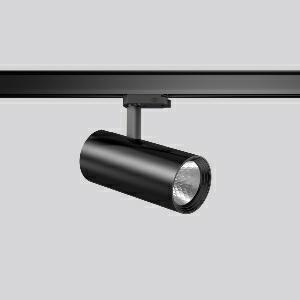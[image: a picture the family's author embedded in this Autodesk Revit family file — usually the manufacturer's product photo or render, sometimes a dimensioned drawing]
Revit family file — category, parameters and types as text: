
# Revit family: deecos_s_mini_742196_003_76_2dde
name_source: partatom
category: Lighting Fixtures
units: mm (PartAtom-declared; Revit-internal decimal feet)

## family parameters
Cut with Voids When Loaded = No
Host = Face
Light Source = No
Part Type = Normal
Room Calculation Point = No
Round Connector Dimension = Use Diameter
Shared = No

## types (1)
- DEECOS S mini (1 x LED Modul 930, 2450 lm, 3000)
    Apparent Load = 20 VA
    Approval mark = CE
    CIE Flux Codes = 99 100 100 100 100
    Color Rendering = 90
    Color Temperature = 3000
    Default Elevation = 1800 mm
    Description = Series: DEECOS S mini
LED surface-mounted projector in modern design with no visible cooling ribs. Housing: die-cast aluminium, powder-coated. Rotation range: 356°. Swivel range: 90°. Black plastic ring and recessed LED to prevent glare from the side. Optical assembly with reflector made of MIRO-Silver with 98% total light reflection for outstanding efficiency - can be changed without tools. Best colour rendering index Ra>90. With adapter for RZB 3-circuit DALI tracks. Suitable for Track on ceiling, Wall track. High quality converter without flickering and stroboscopic effect. The following accessories can be mounted without use of tools: interchangeable lenses, decorative glasses, honeycomb louvre, clear and frosted diffusers, white interchangeable plastic ring. 
Colour: deep black, matt (RAL 9005)
Diameter: 87 mm
Height: 214 mm
Lamp: LED
Socket: without socket
Colour temperature: 3000K
Colour rendering index (CRI): 92
System power: 20 W
Rated luminous flux: 2450 lm
Luminous efficiency: 123 lm/W
Control gear: Converter, dimmable, DALI
Protection class: I
Type of protection: IP 20
    Height = 214 mm
    Lamp = 1 x LED Modul 930
    Lamp Light Flux = 2450 lm
    Lamp count = 1
    Length = 87 mm
    Lifetime = 50000 h
    Luminous efficacy = 123 lm/W
    Manufacturer = RZB
    ModVariant = No
    Model = 742196.003.76
    Mounting Place = Ceiling
    Mounting Type = Rail mounted
    Number of Poles = 1
    OnlyDefault = Yes
    Power Factor = 1
    Product Name = DEECOS S mini
    Product group = Track mounted projectors
    ProductGroupID = 301
    Protection Class = Protection class I
    Protection Degree = IP 20
    RLX_Detail_Level = 1
    RLX_Emergency_Light_Flux = 0 lm
    RLX_Emergency_Type = 0
    RLX_Emergency_Type_DB = No
    RlxData = <blob elided: 38585 chars, md5=1866fb57>
    Socket = socket
    Standby Power = 0 W
    System Light Flux = 2450 lm
    System Power = 20 W
    Type Comments = Product without accessories
    Type Image = 741926.003.jpg
    URL = http://relux.com
    VarID = ---
    Voltage = 230 V
    Voltage Range = 220-240 V
    Weight = 0.00 kg
    Width = 0 mm  [stored 0 ft]

note: [stored X ft] marks values corroborated as IEEE doubles in the binary element streams (Revit-internal decimal feet)

## geometry (parser evidence)
native form markers: Blend x4, Sweep x13
no freeform markers — native parametric forms only
